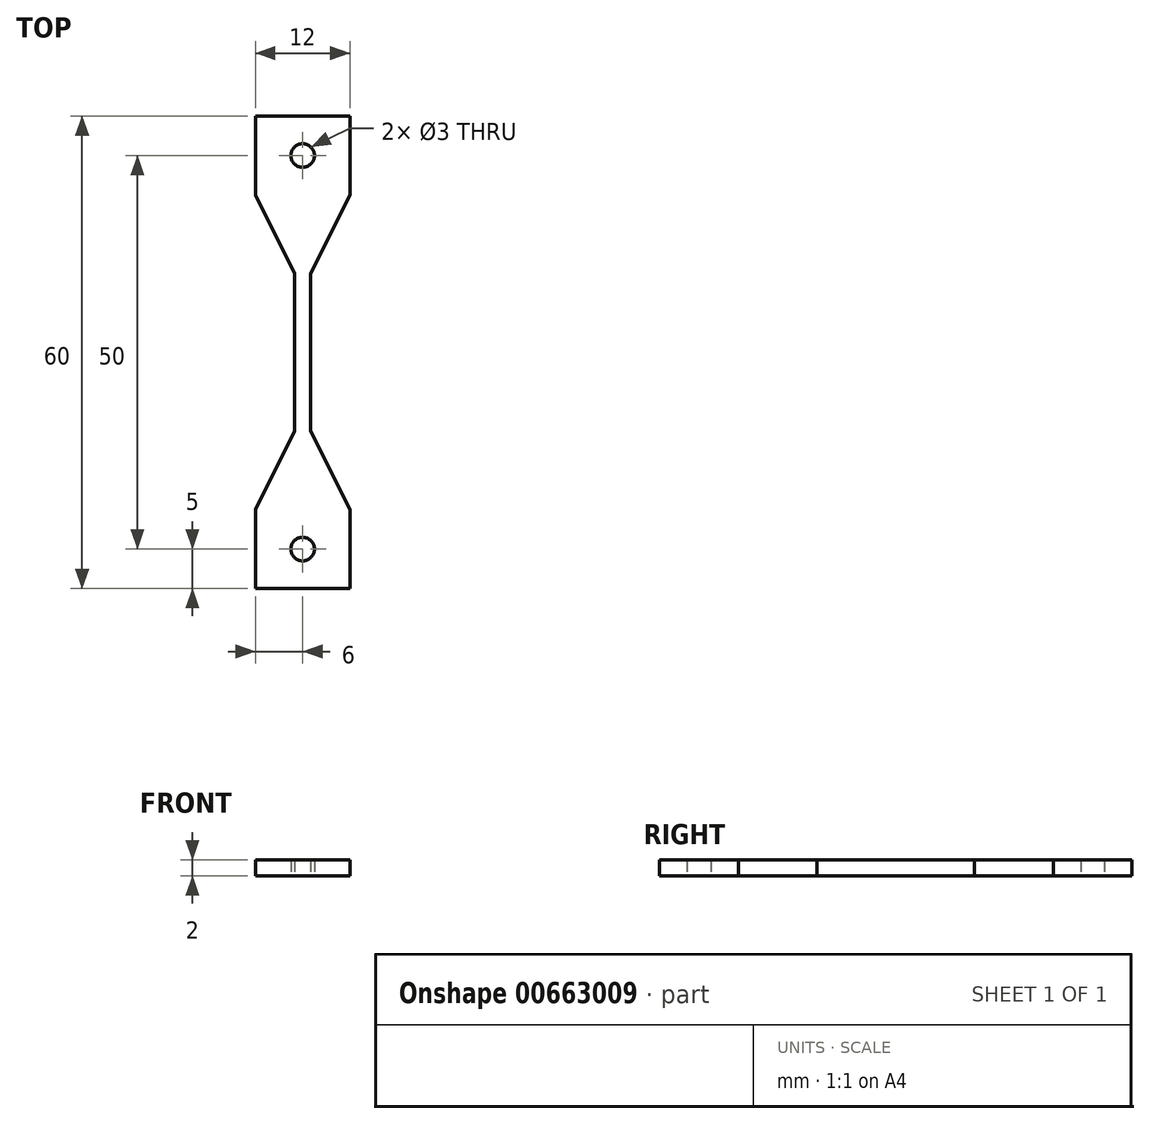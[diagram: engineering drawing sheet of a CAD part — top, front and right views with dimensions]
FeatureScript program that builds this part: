
annotation { "Feature Type Name" : "Feature", "Feature Type Description" : "" }
export const myFeature = defineFeature(function(context is Context, id is Id, definition is map)
    precondition{}
    {
        {
            var Q0;
            Q0=qCreatedBy(makeId("Top.planeOp"),FACE);
            var sketch = newSketch(context, id + "F0", { "sketchPlane" : qUnion([Q0])});
            skLineSegment(sketch, "E0", {"start": v(0, 0) * mm, "end": v(12, 0) * mm});
            skLineSegment(sketch, "E1", {"start": v(12, 0) * mm, "end": v(12, 10) * mm});
            skLineSegment(sketch, "E2", {"start": v(12, 10) * mm, "end": v(7, 20) * mm});
            skLineSegment(sketch, "E3", {"start": v(7, 20) * mm, "end": v(7, 40) * mm});
            skLineSegment(sketch, "E4", {"start": v(7, 40) * mm, "end": v(12, 50) * mm});
            skLineSegment(sketch, "E5", {"start": v(12, 50) * mm, "end": v(12, 60) * mm});
            skLineSegment(sketch, "E6", {"start": v(12, 60) * mm, "end": v(0, 60) * mm});
            skLineSegment(sketch, "E7", {"start": v(0, 60) * mm, "end": v(0, 50) * mm});
            skLineSegment(sketch, "E8", {"start": v(0, 50) * mm, "end": v(5, 40) * mm});
            skLineSegment(sketch, "E9", {"start": v(5, 40) * mm, "end": v(5, 20) * mm});
            skLineSegment(sketch, "E10", {"start": v(5, 20) * mm, "end": v(0, 10) * mm});
            skLineSegment(sketch, "E11", {"start": v(0, 10) * mm, "end": v(0, 0) * mm});
            skCircle(sketch, "E12", {"center": v(6, 55) * mm, "radius": 1.5 * mm});
            skCircle(sketch, "E13", {"center": v(6, 5) * mm, "radius": 1.5 * mm});
            skSolve(sketch);
        }
        {
            var Q0;
            Q0=makeQuery(id+"F0.imprint","IMPRINT",FACE,{"disambiguationData":[TD([[makeQuery(id+"F0.imprint","IMPRINT",EDGE,{"derivedFrom":sQuery(id+"F0.wireOp",EDGE,"E0")}),1.0]])]});
            extrude(context, id + "F1", {"entities" : qUnion([Q0]), "depth" : 2 * mm, "offsetDistance" : 25 * mm});
        }
    });
